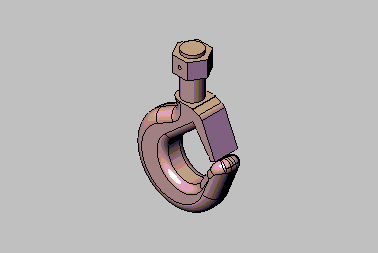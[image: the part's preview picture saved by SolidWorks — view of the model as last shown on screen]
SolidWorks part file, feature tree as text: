
SOLIDWORKS PART (.sldprt)
format: sldprt  version: not decoded by parser v0  size: 987,136 bytes
history: native  units: mm
features: plane x5, sketch x4, extrude x3, fillet x2, material x1, mirror x1, cut_extrude x1 (+10 scaffold rows collapsed)
feature tree (27):
  scaffold x10  (default folders/planes/origin — collapsed)
  material  "Material <not specified>"
  plane  "Plane1"  Offset=0mm
  plane  "Plane2"  Offset=0mm
  plane  "Plane3"  Offset=0mm
  sketch  "Sketch1"
  extrude  "Extrude1"  Depth=23.8125mm
  fillet  "Fillet1"  Radius=19.05mm
  fillet  "Fillet2"  Radius=11.90625mm
  mirror  "Mirror1"
  sketch  "Sketch2"  dims[D1=38.1mm]
  extrude  "Extrude2"  Depth=85.725mm
  plane  "Plane4"  Offset=0mm
  plane  "Plane5"  Offset=47.625mm
  sketch  "Sketch3"  dims[D1=53.975mm]
  extrude  "Extrude3"  Depth=32.54375mm
  sketch  "Sketch4"  dims[D1=6.35mm D2=~16.271875mm]
  cut_extrude  "Cut-Extrude2"  [1 undecoded]
decode coverage: 8 of 11 modeling features carry decoded parameters
note: ~ marks probable driven/reference dimensions
note: 1 parameter value undecoded
note: suppression state not decoded; provenance and decode notes live in map.json
